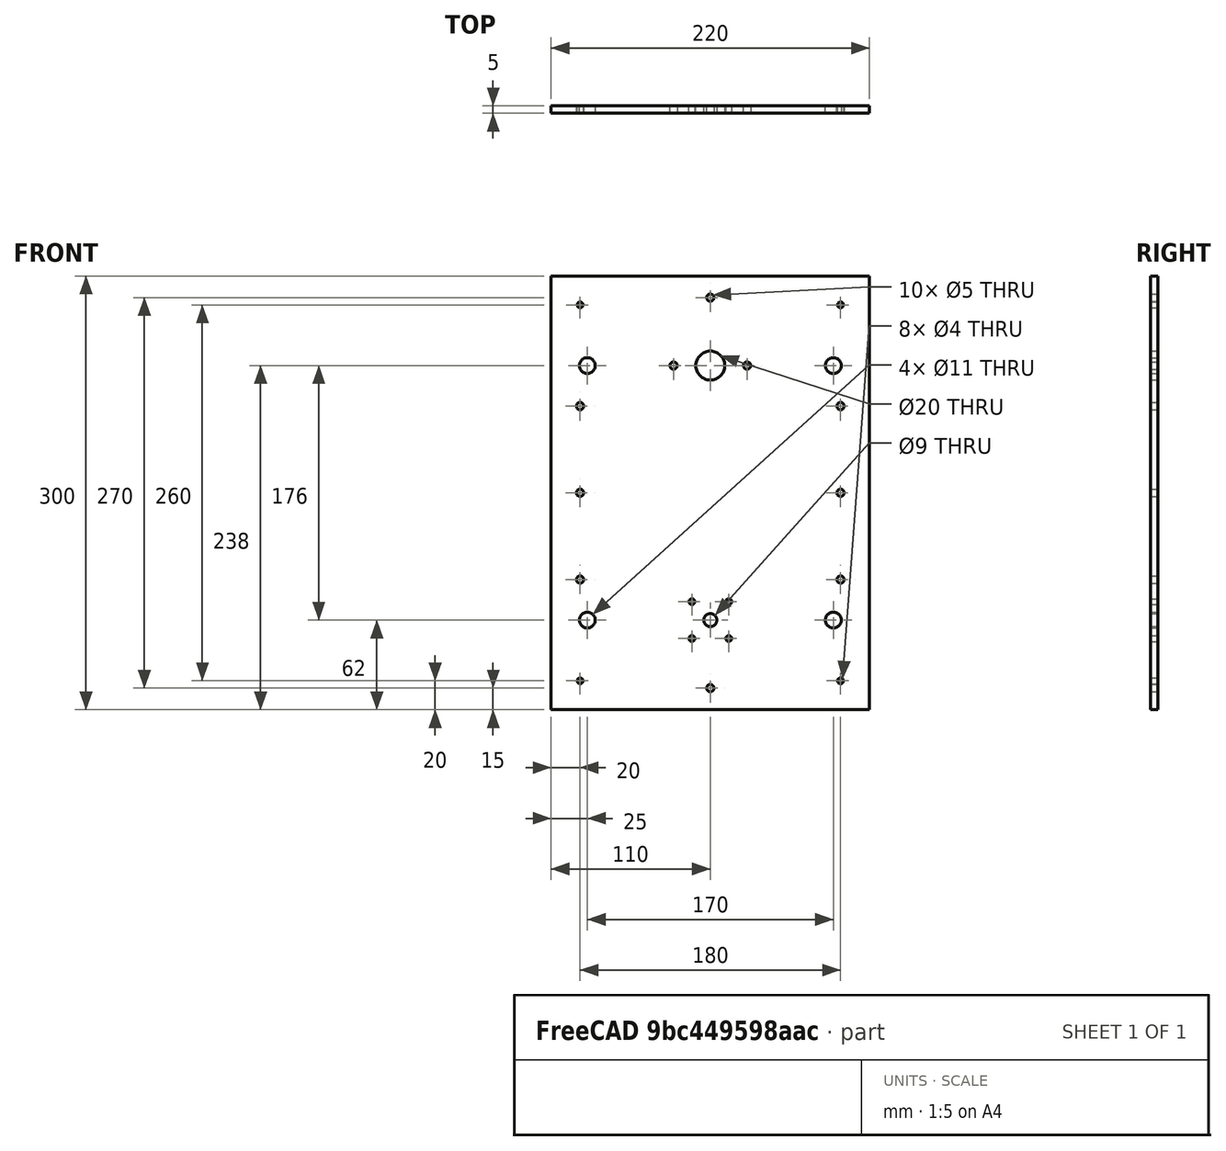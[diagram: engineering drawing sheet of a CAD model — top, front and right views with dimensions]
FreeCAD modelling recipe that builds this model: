
FCSTD DOCUMENT  (FreeCAD 0.20R29603 (Git))
Label: BallenMachineV2
License: All rights reserved
LicenseURL: http://en.wikipedia.org/wiki/All_rights_reserved
objects: Sketcher::SketchObject×1, PartDesign::Pad×1, PartDesign::Body×1
note: 4 computed .brp shape members not serialized (recipe doc carries the construction recipe); baked Part::Feature solids carry a one-line shape summary decoded from their .brp

FEATURE [Sketcher::SketchObject] Sketch
  FullyConstrained = true
  MapMode = 5
  Placement = pos=(0,0,0) rot=(1,0,0;1.5708rad)
  Support = -> [XZ_Plane]
  sketch-geometry (29):
    g0: LineSegment StartX=-110 StartY=150 StartZ=0 EndX=-110 EndY=-150 EndZ=0
    g1: LineSegment StartX=-110 StartY=-150 StartZ=0 EndX=110 EndY=-150 EndZ=0
    g2: LineSegment StartX=110 StartY=-150 StartZ=0 EndX=110 EndY=150 EndZ=0
    g3: LineSegment StartX=110 StartY=150 StartZ=0 EndX=-110 EndY=150 EndZ=0
    g4: GeomPoint X=0 Y=0 Z=0
    g5: Circle CenterX=0 CenterY=88 CenterZ=0 NormalX=0 NormalY=0 NormalZ=1 AngleXU=0 Radius=10
    g6: Circle CenterX=25.4 CenterY=88 CenterZ=0 NormalX=0 NormalY=0 NormalZ=1 AngleXU=0 Radius=2.5
    g7: Circle CenterX=-25.4 CenterY=88 CenterZ=0 NormalX=0 NormalY=0 NormalZ=1 AngleXU=0 Radius=2.5
    g8: Circle CenterX=85 CenterY=88 CenterZ=0 NormalX=0 NormalY=0 NormalZ=1 AngleXU=0 Radius=5.5
    g9: Circle CenterX=-85 CenterY=88 CenterZ=0 NormalX=0 NormalY=0 NormalZ=1 AngleXU=0 Radius=5.5
    g10: Circle CenterX=-85 CenterY=-88 CenterZ=0 NormalX=0 NormalY=0 NormalZ=1 AngleXU=0 Radius=5.5
    g11: Circle CenterX=85 CenterY=-88 CenterZ=0 NormalX=0 NormalY=0 NormalZ=1 AngleXU=0 Radius=5.5
    g12: Circle CenterX=-90 CenterY=130 CenterZ=0 NormalX=0 NormalY=0 NormalZ=1 AngleXU=0 Radius=2
    g13: Circle CenterX=90 CenterY=130 CenterZ=0 NormalX=0 NormalY=0 NormalZ=1 AngleXU=0 Radius=2
    g14: Circle CenterX=-90 CenterY=-130 CenterZ=0 NormalX=0 NormalY=0 NormalZ=1 AngleXU=0 Radius=2
    g15: Circle CenterX=90 CenterY=-130 CenterZ=0 NormalX=0 NormalY=0 NormalZ=1 AngleXU=0 Radius=2
    g16: Circle CenterX=0 CenterY=135 CenterZ=0 NormalX=0 NormalY=0 NormalZ=1 AngleXU=0 Radius=2.5
    g17: Circle CenterX=0 CenterY=-135 CenterZ=0 NormalX=0 NormalY=0 NormalZ=1 AngleXU=0 Radius=2.5
    g18: Circle CenterX=90 CenterY=0 CenterZ=0 NormalX=0 NormalY=0 NormalZ=1 AngleXU=0 Radius=2.5
    g19: Circle CenterX=-90 CenterY=0 CenterZ=0 NormalX=0 NormalY=0 NormalZ=1 AngleXU=0 Radius=2.5
    g20: Circle CenterX=-90 CenterY=-60 CenterZ=0 NormalX=0 NormalY=0 NormalZ=1 AngleXU=0 Radius=2.5
    g21: Circle CenterX=-90 CenterY=60 CenterZ=0 NormalX=0 NormalY=0 NormalZ=1 AngleXU=0 Radius=2.5
    g22: Circle CenterX=90 CenterY=60 CenterZ=0 NormalX=0 NormalY=0 NormalZ=1 AngleXU=0 Radius=2.5
    g23: Circle CenterX=90 CenterY=-60 CenterZ=0 NormalX=0 NormalY=0 NormalZ=1 AngleXU=0 Radius=2.5
    g24: Circle CenterX=0 CenterY=-88 CenterZ=0 NormalX=0 NormalY=0 NormalZ=1 AngleXU=0 Radius=4.5
    g25: Circle CenterX=12.75 CenterY=-75.25 CenterZ=0 NormalX=0 NormalY=0 NormalZ=1 AngleXU=0 Radius=2
    g26: Circle CenterX=-12.75 CenterY=-75.25 CenterZ=0 NormalX=0 NormalY=0 NormalZ=1 AngleXU=0 Radius=2
    g27: Circle CenterX=-12.75 CenterY=-100.75 CenterZ=0 NormalX=0 NormalY=0 NormalZ=1 AngleXU=0 Radius=2
    g28: Circle CenterX=12.75 CenterY=-100.75 CenterZ=0 NormalX=0 NormalY=0 NormalZ=1 AngleXU=0 Radius=2
  constraints (84):
    c: Coincident(g0,g1)
    c: Coincident(g1,g2)
    c: Coincident(g2,g3)
    c: Coincident(g3,g0)
    c: Horizontal(g1)
    c: Horizontal(g3)
    c: Vertical(g0)
    c: Vertical(g2)
    c: Symmetric(g1,g0,g4)
    c: Coincident(g4,g-1)
    c: DistanceX(g1,g1) = 220
    c: DistanceY(g2,g2) = 300
    c: Diameter(g5) = 20
    c: DistanceX(g4,g5) = 0
    c: DistanceY(g4,g5) = 88
    c: Diameter(g6) = 5
    c: DistanceX(g5,g6) = 25.4
    c: DistanceY(g6,g5) = 0
    c: Diameter(g7) = 5
    c: DistanceY(g7,g5) = 0
    c: DistanceX(g7,g5) = 25.4
    c: Diameter(g8) = 11
    c: DistanceX(g5,g8) = 85
    c: DistanceY(g5,g8) = 0
    c: Diameter(g9) = 11
    c: DistanceX(g9,g5) = 85
    c: DistanceY(g5,g9) = 0
    c: Diameter(g10) = 11
    c: DistanceX(g10,g4) = 85
    c: DistanceY(g10,g4) = 88
    c: Diameter(g11) = 11
    c: DistanceY(g10,g11) = 0
    c: DistanceX(g4,g11) = 85
    c: Diameter(g12) = 4
    c: DistanceX(g12,g4) = 90
    c: DistanceY(g4,g12) = 130
    c: Diameter(g13) = 4
    c: DistanceY(g12,g13) = 0
    c: DistanceX(g4,g13) = 90
    c: Diameter(g14) = 4
    c: DistanceX(g14,g12) = 0
    c: DistanceY(g14,g4) = 130
    c: Diameter(g15) = 4
    c: DistanceY(g14,g15) = 0
    c: DistanceX(g15,g13) = 0
    c: Diameter(g16) = 5
    c: DistanceX(g16,g4) = 0
    c: DistanceY(g4,g16) = 135
    c: Diameter(g17) = 5
    c: DistanceX(g17,g4) = 0
    c: DistanceY(g17,g4) = 135
    c: Diameter(g18) = 5
    c: DistanceX(g4,g18) = 90
    c: DistanceY(g4,g18) = 0
    c: Diameter(g19) = 5
    c: DistanceX(g19,g4) = 90
    c: DistanceY(g4,g19) = 0
    c: Diameter(g20) = 5
    c: DistanceX(g20,g19) = 0
    c: DistanceY(g20,g19) = 60
    c: Diameter(g21) = 5
    c: DistanceX(g21,g19) = 0
    c: DistanceY(g19,g21) = 60
    c: Diameter(g22) = 5
    c: DistanceY(g18,g22) = 60
    c: DistanceX(g22,g18) = 0
    c: Diameter(g23) = 5
    c: DistanceX(g18,g23) = 0
    c: DistanceY(g23,g18) = 60
    c: DistanceX(g4,g24) = 0
    c: Diameter(g24) = 9
    c: DistanceY(g24,g4) = 88
    c: Diameter(g25) = 4
    c: DistanceX(g24,g25) = 12.75
    c: DistanceY(g24,g25) = 12.75
    c: Diameter(g26) = 4
    c: DistanceX(g26,g24) = 12.75
    c: DistanceY(g24,g26) = 12.75
    c: Diameter(g27) = 4
    c: DistanceX(g27,g24) = 12.75
    c: DistanceY(g27,g24) = 12.75
    c: Diameter(g28) = 4
    c: DistanceX(g24,g28) = 12.75
    c: DistanceY(g28,g24) = 12.75
FEATURE [PartDesign::Pad] Pad
  Direction = (0,-1,2e-16)
  Length = 5
  Length2 = 10
  Placement = pos=(0,0,0) rot=(1,0,0;1.5708rad)
  Profile = -> Sketch
  ReferenceAxis = -> Sketch [N_Axis]
  Type = 0
FEATURE [PartDesign::Body] Body
  Group = -> [Sketch,Pad]
  Origin = -> Origin
  Tip = -> Pad
